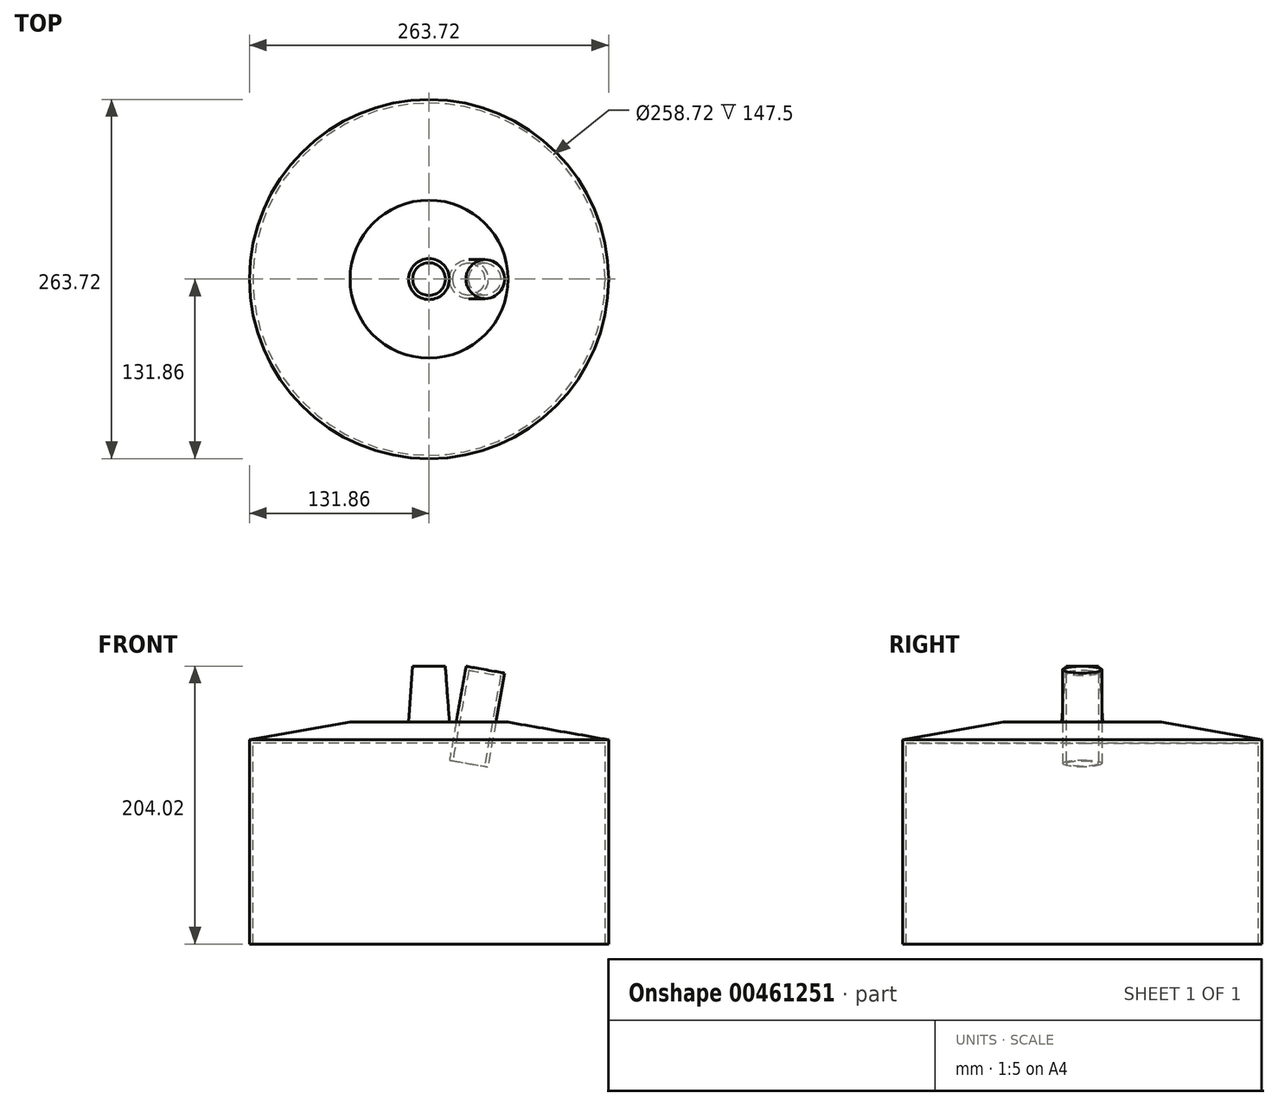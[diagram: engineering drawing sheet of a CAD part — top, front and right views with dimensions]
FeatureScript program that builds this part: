
annotation { "Feature Type Name" : "Feature", "Feature Type Description" : "" }
export const myFeature = defineFeature(function(context is Context, id is Id, definition is map)
    precondition{}
    {
        {
            var Q0;
            Q0=qCreatedBy(makeId("Front.planeOp"),FACE);
            var sketch = newSketch(context, id + "F0", { "sketchPlane" : qUnion([Q0])});
            skLineSegment(sketch, "E0", {"start": v(0, 63.67) * mm, "end": v(-13, 63.67) * mm});
            skLineSegment(sketch, "E1", {"start": v(-13, 63.67) * mm, "end": v(-13, 23.67) * mm});
            skLineSegment(sketch, "E2", {"start": v(-13, 23.67) * mm, "end": v(-28, 23.67) * mm});
            skLineSegment(sketch, "E3", {"start": v(-28, 23.67) * mm, "end": v(-37, 63.67) * mm});
            skLineSegment(sketch, "E4", {"start": v(-37, 63.67) * mm, "end": v(-58, 63.67) * mm});
            skLineSegment(sketch, "E5", {"start": v(-58, 63.67) * mm, "end": v(-58, 12.67) * mm});
            skLineSegment(sketch, "E6", {"start": v(0, 63.67) * mm, "end": v(13, 63.67) * mm});
            skLineSegment(sketch, "E7", {"start": v(13, 63.67) * mm, "end": v(13, 23.67) * mm});
            skLineSegment(sketch, "E8", {"start": v(13, 23.67) * mm, "end": v(28, 23.67) * mm});
            skLineSegment(sketch, "E9", {"start": v(28, 23.67) * mm, "end": v(37, 63.67) * mm});
            skLineSegment(sketch, "E10", {"start": v(37, 63.67) * mm, "end": v(58, 63.67) * mm});
            skLineSegment(sketch, "E11", {"start": v(58, 63.67) * mm, "end": v(58, 12.67) * mm});
            skLineSegment(sketch, "E12", {"start": v(-58, 12.67) * mm, "end": v(-131.86, -0.35) * mm});
            skLineSegment(sketch, "E13", {"start": v(58, 12.67) * mm, "end": v(131.86, -0.35) * mm});
            skLineSegment(sketch, "E14", {"start": v(-131.86, -0.35) * mm, "end": v(131.86, -0.35) * mm});
            skLineSegment(sketch, "E15", {"start": v(-131.86, -0.35) * mm, "end": v(-131.86, -150.35) * mm});
            skLineSegment(sketch, "E16", {"start": v(131.86, -0.35) * mm, "end": v(131.86, -150.35) * mm});
            skLineSegment(sketch, "E17", {"start": v(-131.86, -150.35) * mm, "end": v(131.86, -150.35) * mm});
            skLineSegment(sketch, "E18", {"start": v(0, 0) * mm, "end": v(0, -150.35) * mm});
            skLineSegment(sketch, "E19", {"start": v(0, -150.35) * mm, "end": v(0, 0) * mm});
            skLineSegment(sketch, "E20", {"start": v(0, 63.67) * mm, "end": v(0, 0) * mm});
            skSolve(sketch);
        }
        {
            var Q0;
            {var subQ0=sQuery(id+"F0.wireOp",EDGE,"E16");Q0=makeQuery(id+"F0.imprint","IMPRINT",FACE,{"disambiguationData":[TD([[makeQuery(id+"F0.imprint","IMPRINT",EDGE,{"derivedFrom":subQ0}),-1.0]])]});}
            var Q1;
            Q1=sQuery(id+"F0.wireOp",EDGE,"E18");
            revolve(context, id + "F1", {"entities" : qUnion([Q0]), "axis" : qUnion([Q1]), "revolveType" : RevolveType.FULL});
        }
        {
            var Q0;
            Q0=qCreatedBy(makeId("Front.planeOp"),FACE);
            var sketch = newSketch(context, id + "F2", { "sketchPlane" : qUnion([Q0])});
            skLineSegment(sketch, "E21", {"start": v(0, 63.67) * mm, "end": v(-13, 63.67) * mm});
            skLineSegment(sketch, "E22", {"start": v(-13, 63.67) * mm, "end": v(-13, 23.67) * mm});
            skLineSegment(sketch, "E23", {"start": v(-13, 23.67) * mm, "end": v(-28, 23.67) * mm});
            skLineSegment(sketch, "E24", {"start": v(-28, 23.67) * mm, "end": v(-37, 63.67) * mm});
            skLineSegment(sketch, "E25", {"start": v(-37, 63.67) * mm, "end": v(-58, 63.67) * mm});
            skLineSegment(sketch, "E26", {"start": v(-58, 63.67) * mm, "end": v(-58, 12.67) * mm});
            skLineSegment(sketch, "E27", {"start": v(0, 63.67) * mm, "end": v(13, 63.67) * mm});
            skLineSegment(sketch, "E28", {"start": v(13, 63.67) * mm, "end": v(13, 23.67) * mm});
            skLineSegment(sketch, "E29", {"start": v(13, 23.67) * mm, "end": v(28, 23.67) * mm});
            skLineSegment(sketch, "E30", {"start": v(28, 23.67) * mm, "end": v(37, 63.67) * mm});
            skLineSegment(sketch, "E31", {"start": v(37, 63.67) * mm, "end": v(58, 63.67) * mm});
            skLineSegment(sketch, "E32", {"start": v(58, 63.67) * mm, "end": v(58, 12.67) * mm});
            skLineSegment(sketch, "E33", {"start": v(-58, 12.67) * mm, "end": v(-131.86, -0.35) * mm});
            skLineSegment(sketch, "E34", {"start": v(58, 12.67) * mm, "end": v(131.86, -0.35) * mm});
            skLineSegment(sketch, "E35", {"start": v(0, -0.35) * mm, "end": v(131.86, -0.35) * mm});
            skLineSegment(sketch, "E36", {"start": v(-131.86, -0.35) * mm, "end": v(-131.86, -150.35) * mm});
            skLineSegment(sketch, "E37", {"start": v(131.86, -0.35) * mm, "end": v(131.86, -150.35) * mm});
            skLineSegment(sketch, "E38", {"start": v(-131.86, -150.35) * mm, "end": v(131.86, -150.35) * mm});
            skLineSegment(sketch, "E39", {"start": v(0, 0) * mm, "end": v(0, -150.35) * mm});
            skLineSegment(sketch, "E40", {"start": v(0, -150.35) * mm, "end": v(0, 0) * mm});
            skLineSegment(sketch, "E41", {"start": v(0, 63.67) * mm, "end": v(0, 0) * mm});
            skLineSegment(sketch, "E42", {"start": v(-58, 12.67) * mm, "end": v(-58, 0) * mm});
            skLineSegment(sketch, "E43", {"start": v(-58, 0) * mm, "end": v(-131.86, -0.35) * mm});
            skLineSegment(sketch, "E44", {"start": v(-58, 12.67) * mm, "end": v(0, 12.67) * mm});
            skLineSegment(sketch, "E45", {"start": v(0, 12.67) * mm, "end": v(0, 0) * mm});
            skLineSegment(sketch, "E46", {"start": v(-58, 0) * mm, "end": v(0, 0) * mm});
            skSolve(sketch);
        }
        {
            var Q0;
            Q0=makeQuery(id+"F1.opRevolve","SWEPT_FACE",FACE,{"disambiguationData":[OSD([sQuery(id+"F0.wireOp",EDGE,"E14")])]});
            var Q1;
            Q1=sQuery(id+"F2.wireOp",VERTEX,"E34.start");
            cPlane(context, id + "F3", {"entities" : qUnion([Q0, Q1]), "cplaneType" : CPlaneType.PLANE_POINT, "offset" : 25 * mm, "width" : 150 * mm, "height" : 150 * mm});
        }
        {
            var Q0;
            Q0=makeQuery(id+"F2.imprint","IMPRINT",FACE,{"disambiguationData":[TD([[makeQuery(id+"F2.imprint","IMPRINT",EDGE,{"derivedFrom":sQuery(id+"F2.wireOp",EDGE,"E33")}),1.0]])]});
            var Q1;
            Q1=makeQuery(id+"F2.imprint","IMPRINT",FACE,{"disambiguationData":[TD([[makeQuery(id+"F2.imprint","IMPRINT",EDGE,{"derivedFrom":sQuery(id+"F2.wireOp",EDGE,"E42")}),1.0]])]});
            var Q2;
            Q2=sQuery(id+"F2.wireOp",EDGE,"E41");
            revolve(context, id + "F4", {"entities" : qUnion([Q0, Q1]), "axis" : qUnion([Q2]), "revolveType" : RevolveType.FULL});
        }
        {
            var Q0;
            Q0=qCreatedBy(id+"F3.planeOp",FACE);
            var sketch = newSketch(context, id + "F5", { "sketchPlane" : qUnion([Q0])});
            skCircle(sketch, "E47", {"center": v(0, 0) * mm, "radius": 15 * mm});
            skSolve(sketch);
        }
        {
            var Q0;
            Q0=qCreatedBy(id+"F3.planeOp",FACE);
            cPlane(context, id + "F6", {"entities" : qUnion([Q0]), "cplaneType" : CPlaneType.OFFSET, "offset" : 41 * mm, "width" : 150 * mm, "height" : 150 * mm});
        }
        {
            var Q0;
            Q0=qCreatedBy(id+"F6.planeOp",FACE);
            var sketch = newSketch(context, id + "F7", { "sketchPlane" : qUnion([Q0])});
            skCircle(sketch, "E48", {"center": v(0, 0) * mm, "radius": 12 * mm});
            skSolve(sketch);
        }
        {
            var Q0;
            Q0=makeQuery(id+"F5.imprint","IMPRINT",FACE,{"disambiguationData":[TD([[makeQuery(id+"F5.imprint","IMPRINT",EDGE,{"derivedFrom":sQuery(id+"F5.wireOp",EDGE,"E47")}),1.0]])]});
            var Q1;
            Q1=makeQuery(id+"F7.imprint","IMPRINT",FACE,{"disambiguationData":[TD([[makeQuery(id+"F7.imprint","IMPRINT",EDGE,{"derivedFrom":sQuery(id+"F7.wireOp",EDGE,"E48")}),1.0]])]});
            loft(context, id + "F8", {"sheetProfilesArray" : [{ "sheetProfileEntities" : qUnion([Q0]) }, { "sheetProfileEntities" : qUnion([Q1]) }]});
        }
        {
            var Q0;
            Q0=makeQuery(id+"F4.opRevolve","SWEPT_FACE",FACE,{"disambiguationData":[OSD([sQuery(id+"F2.wireOp",EDGE,"E44")])]});
            var Q1;
            Q1=sQuery(id+"F0.wireOp",EDGE,"E13");
            cPlane(context, id + "F9", {"entities" : qUnion([Q0, Q1]), "cplaneType" : CPlaneType.LINE_ANGLE, "offset" : 25 * mm, "angle" : 0 * degree, "width" : 150 * mm, "height" : 150 * mm});
        }
        {
            var Q0;
            Q0=qCreatedBy(id+"F9.planeOp",FACE);
            var sketch = newSketch(context, id + "F10", { "sketchPlane" : qUnion([Q0])});
            skCircle(sketch, "E49", {"center": v(31.78, 0) * mm, "radius": 14.34 * mm});
            skSolve(sketch);
        }
        {
            var Q0;
            Q0=makeQuery(id+"F10.imprint","IMPRINT",FACE,{"disambiguationData":[TD([[makeQuery(id+"F10.imprint","IMPRINT",EDGE,{"derivedFrom":sQuery(id+"F10.wireOp",EDGE,"E49")}),1.0]])]});
            extrude(context, id + "F11", {"entities" : qUnion([Q0]), "endBound" : BoundingType.SYMMETRIC, "oppositeDirection" : true, "depth" : 70 * mm});
        }
        {
            var Q0;
            Q0=makeQuery(id+"F1.opRevolve","SWEPT_FACE",FACE,{"disambiguationData":[OSD([sQuery(id+"F0.wireOp",EDGE,"E17")])]});
            shell(context, id + "F12", {"entities" : qUnion([Q0]), "thickness" : 2.5 * mm});
        }
        {
            var Q0;
            Q0=makeQuery(id+"F11.opExtrude","CAP_FACE",FACE,{"disambiguationData":[OSD([sQuery(id+"F10.wireOp",EDGE,"E49")])],"isStart":true});
            shell(context, id + "F13", {"entities" : qUnion([Q0]), "thickness" : 2.5 * mm});
        }
    });
